SOLIDWORKS PART (.sldprt)
format: sldprt  version: not decoded by parser v0  size: 152,064 bytes
history: native  units: mm
features: sketch x3, chamfer x3, extrude x2, material x1, cut_extrude x1 (+13 scaffold rows collapsed)
feature tree (23):
  scaffold x13  (default folders/planes/origin — collapsed)
  material  "Material <not specified>"
  sketch  "Sketch1"  dims[D1=3.1mm D2=9.1mm D3=3.0mm D4=3.0mm D5=1.0mm D6=4.0mm D7=~5.216288mm]
  extrude  "Boss-Extrude1"  Depth=3mm
  sketch  "Sketch2"  dims[c1.D1=~9.405886mm c1.D2=~1.31988mm c2.D1=4.0mm c2.D2=4.0mm]
  extrude  "Boss-Extrude2"  Depth=10mm
  sketch  "Sketch3"
  cut_extrude  "Cut-Extrude1"  [1 undecoded]
  chamfer  "Chamfer1"  Distance=1mm Angle=45deg
  chamfer  "Chamfer2"  Distance=1mm Angle=45deg
  chamfer  "Chamfer3"  Distance=1mm Angle=45deg
decode coverage: 7 of 9 modeling features carry decoded parameters
note: ~ marks probable driven/reference dimensions
note: 1 parameter value undecoded
note: suppression state not decoded; provenance and decode notes live in map.json
